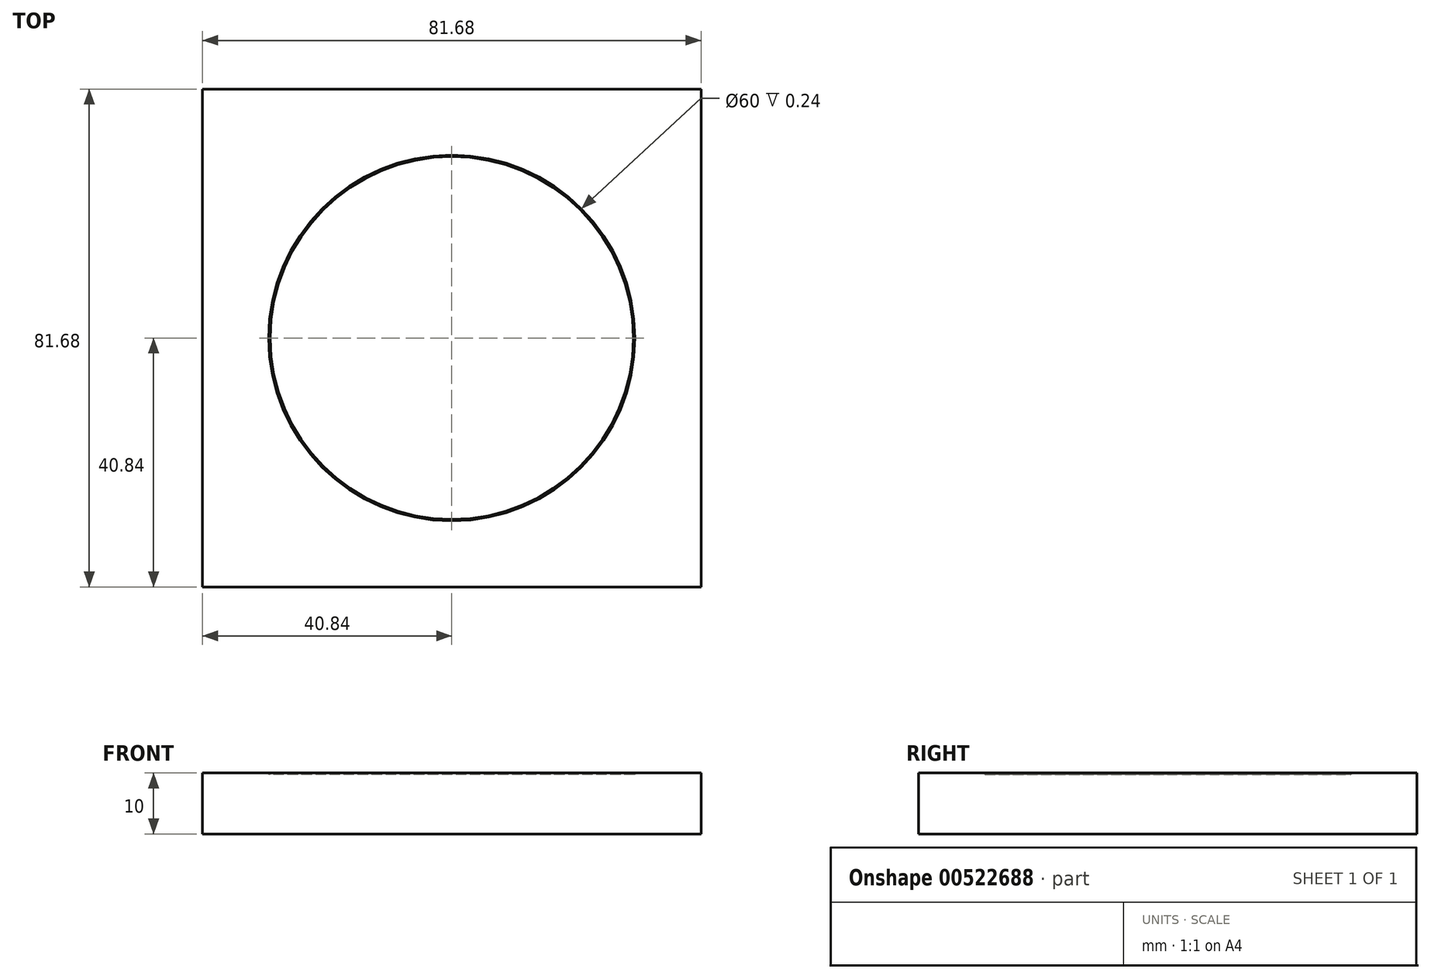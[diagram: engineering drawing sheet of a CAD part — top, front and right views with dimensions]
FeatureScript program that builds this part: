
annotation { "Feature Type Name" : "Feature", "Feature Type Description" : "" }
export const myFeature = defineFeature(function(context is Context, id is Id, definition is map)
    precondition{}
    {
        {
            var Q0;
            Q0=qCreatedBy(makeId("Top.planeOp"),FACE);
            var sketch = newSketch(context, id + "F0", { "sketchPlane" : qUnion([Q0])});
            skLineSegment(sketch, "E0.bottom", {"start": v(40.84, -40.84) * mm, "end": v(-40.84, -40.84) * mm});
            skLineSegment(sketch, "E0.top", {"start": v(40.84, 40.84) * mm, "end": v(-40.84, 40.84) * mm});
            skLineSegment(sketch, "E0.left", {"start": v(40.84, -40.84) * mm, "end": v(40.84, 40.84) * mm});
            skLineSegment(sketch, "E0.right", {"start": v(-40.84, -40.84) * mm, "end": v(-40.84, 40.84) * mm});
            skPoint(sketch, "E0.middle", {"position": v(0, 0) * mm});
            skCircle(sketch, "E1", {"center": v(0, 0) * mm, "radius": 30 * mm});
            skCircle(sketch, "E2", {"center": v(0, 0) * mm, "radius": 29.76 * mm});
            skLineSegment(sketch, "E3", {"start": v(-52.92, 0) * mm, "end": v(48.97, 0) * mm, "construction": true});
            skLineSegment(sketch, "E4", {"start": v(0, 48.79) * mm, "end": v(0, -45.12) * mm, "construction": true});
            skSolve(sketch);
        }
        {
            var Q0;
            Q0=makeQuery(id+"F0.imprint","IMPRINT",FACE,{"disambiguationData":[TD([[makeQuery(id+"F0.imprint","IMPRINT",EDGE,{"derivedFrom":sQuery(id+"F0.wireOp",EDGE,"E1")}),1.0]])]});
            extrude(context, id + "F1", {"entities" : qUnion([Q0]), "depth" : 9.76 * mm, "offsetDistance" : 25 * mm});
        }
        {
            var Q0;
            Q0=makeQuery(id+"F0.imprint","IMPRINT",FACE,{"disambiguationData":[TD([[makeQuery(id+"F0.imprint","IMPRINT",EDGE,{"derivedFrom":sQuery(id+"F0.wireOp",EDGE,"E2")}),1.0]])]});
            var Q1;
            Q1=makeQuery(id+"F0.imprint","IMPRINT",FACE,{"disambiguationData":[TD([[makeQuery(id+"F0.imprint","IMPRINT",EDGE,{"derivedFrom":sQuery(id+"F0.wireOp",EDGE,"E0.bottom")}),-1.0]])]});
            extrude(context, id + "F2", {"entities" : qUnion([Q0, Q1]), "operationType" : NewBodyOperationType.ADD, "depth" : 10 * mm, "offsetDistance" : 25 * mm});
        }
    });
